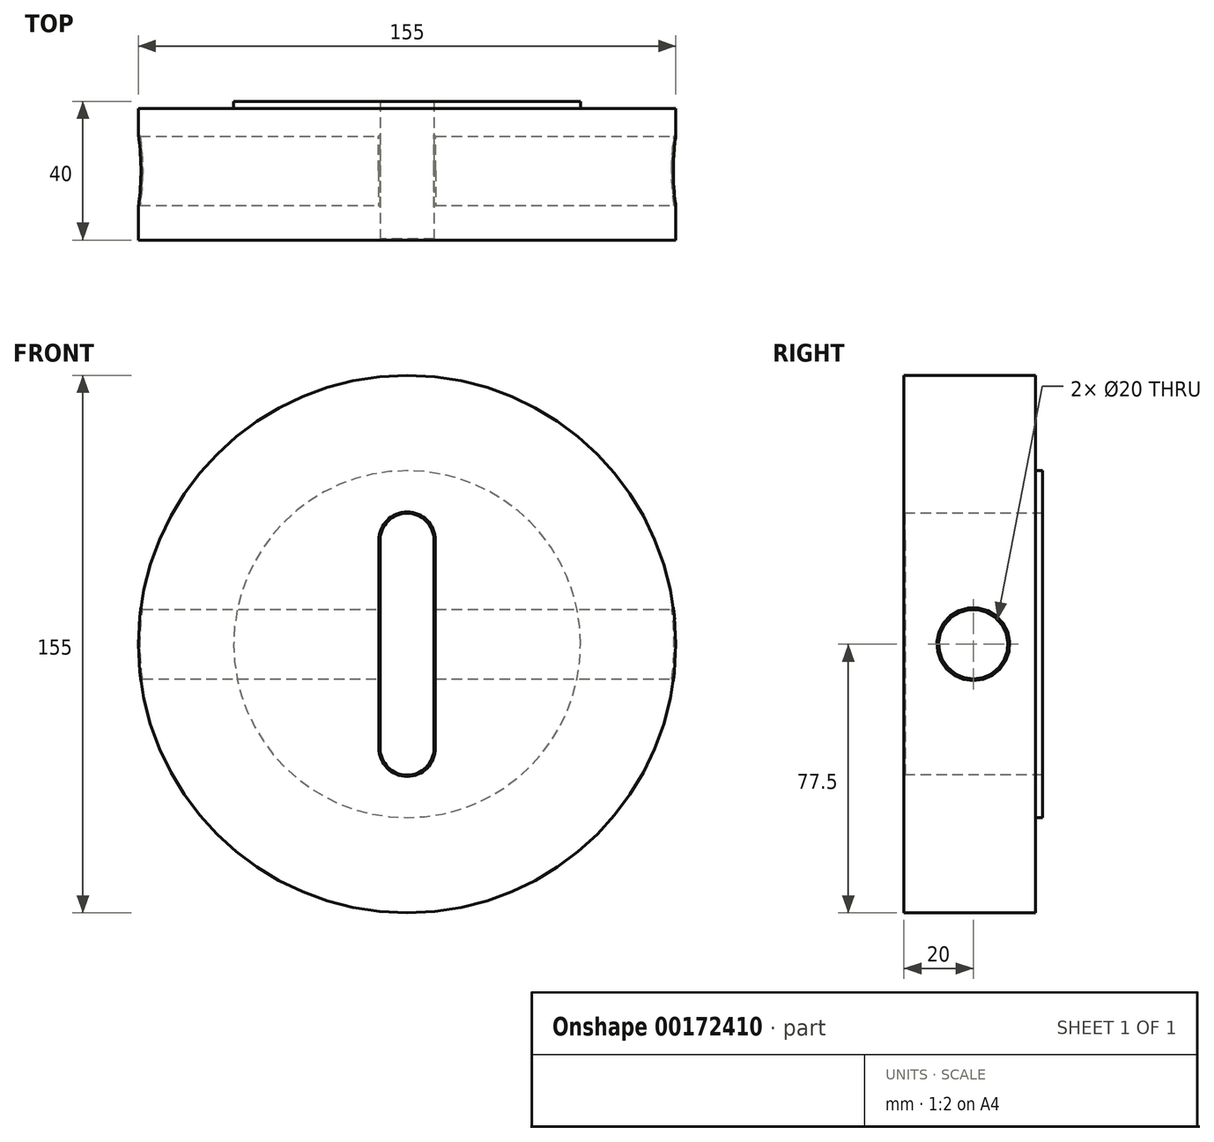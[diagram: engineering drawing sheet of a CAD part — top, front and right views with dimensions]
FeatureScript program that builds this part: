
annotation { "Feature Type Name" : "Feature", "Feature Type Description" : "" }
export const myFeature = defineFeature(function(context is Context, id is Id, definition is map)
    precondition{}
    {
        {
            var Q0;
            Q0=qCreatedBy(makeId("Front.planeOp"),FACE);
            var sketch = newSketch(context, id + "F0", { "sketchPlane" : qUnion([Q0])});
            skCircle(sketch, "E0", {"center": v(0, 0) * mm, "radius": 77.5 * mm});
            skCircle(sketch, "E1", {"center": v(0, 0) * mm, "radius": 50 * mm});
            skLineSegment(sketch, "E2", {"start": v(0, 0) * mm, "end": v(0, 30) * mm, "construction": true});
            skLineSegment(sketch, "E3", {"start": v(0, 0) * mm, "end": v(0, -30) * mm, "construction": true});
            skArc(sketch, "E4", {"start": v(7.75, 30) * mm, "mid": v(0, 37.75) * mm, "end": v(-7.75, 30) * mm});
            skArc(sketch, "E5", {"start": v(7.75, -30) * mm, "mid": v(0, -37.75) * mm, "end": v(-7.75, -30) * mm});
            skLineSegment(sketch, "E6", {"start": v(-7.75, 30) * mm, "end": v(-7.75, -30) * mm});
            skLineSegment(sketch, "E7", {"start": v(7.75, 30) * mm, "end": v(7.75, -30) * mm});
            skSolve(sketch);
        }
        {
            var Q0;
            Q0=makeQuery(id+"F0.imprint","IMPRINT",FACE,{"disambiguationData":[TD([[makeQuery(id+"F0.imprint","IMPRINT",EDGE,{"derivedFrom":sQuery(id+"F0.wireOp",EDGE,"E0")}),1.0]])]});
            extrude(context, id + "F1", {"entities" : qUnion([Q0]), "oppositeDirection" : true, "depth" : 38 * mm});
        }
        {
            var Q0;
            Q0=makeQuery(id+"F0.imprint","IMPRINT",FACE,{"disambiguationData":[TD([[makeQuery(id+"F0.imprint","IMPRINT",EDGE,{"derivedFrom":sQuery(id+"F0.wireOp",EDGE,"E1")}),1.0]])]});
            extrude(context, id + "F2", {"entities" : qUnion([Q0]), "operationType" : NewBodyOperationType.ADD, "oppositeDirection" : true, "depth" : 40 * mm});
        }
        {
            var Q0;
            Q0=qCreatedBy(makeId("Right.planeOp"),FACE);
            var sketch = newSketch(context, id + "F3", { "sketchPlane" : qUnion([Q0])});
            skCircle(sketch, "E8", {"center": v(20, 0) * mm, "radius": 10 * mm});
            skSolve(sketch);
        }
        {
            var Q0;
            Q0=makeQuery(id+"F3.imprint","IMPRINT",FACE,{"disambiguationData":[TD([[makeQuery(id+"F3.imprint","IMPRINT",EDGE,{"derivedFrom":sQuery(id+"F3.wireOp",EDGE,"E8")}),1.0]])]});
            extrude(context, id + "F4", {"entities" : qUnion([Q0]), "operationType" : NewBodyOperationType.REMOVE, "endBound" : BoundingType.THROUGH_ALL, "oppositeDirection" : true, "depth" : 25 * mm, "hasSecondDirection" : true, "secondDirectionBound" : SecondDirectionBoundingType.THROUGH_ALL, "secondDirectionOppositeDirection" : false, "secondDirectionDepth" : 25 * mm});
        }
        {
            var Q0;
            Q0=makeQuery(id+"F4.boolean.opBoolean","INTERSECT",EDGE,{"derivedFrom":[makeQuery(id+"F2.opExtrude","SWEPT_FACE",FACE,{"disambiguationData":[OSD([sQuery(id+"F0.wireOp",EDGE,"E7")])]}),makeQuery(id+"F4.opExtrude","SWEPT_FACE",FACE,{"disambiguationData":[OSD([sQuery(id+"F3.wireOp",EDGE,"E8")])]})]});
            var Q1;
            Q1=makeQuery(id+"F4.boolean.opBoolean","INTERSECT",EDGE,{"disambiguationData":[OD(1.0)],"derivedFrom":[makeQuery(id+"F1.opExtrude","SWEPT_FACE",FACE,{"disambiguationData":[OSD([sQuery(id+"F0.wireOp",EDGE,"E0")])]}),makeQuery(id+"F4.opExtrude","SWEPT_FACE",FACE,{"disambiguationData":[OSD([sQuery(id+"F3.wireOp",EDGE,"E8")])]})]});
            var Q2;
            Q2=makeQuery(id+"F4.boolean.opBoolean","INTERSECT",EDGE,{"derivedFrom":[makeQuery(id+"F2.opExtrude","SWEPT_FACE",FACE,{"disambiguationData":[OSD([sQuery(id+"F0.wireOp",EDGE,"E6")])]}),makeQuery(id+"F4.opExtrude","SWEPT_FACE",FACE,{"disambiguationData":[OSD([sQuery(id+"F3.wireOp",EDGE,"E8")])]})]});
            var Q3;
            Q3=makeQuery(id+"F4.boolean.opBoolean","INTERSECT",EDGE,{"disambiguationData":[OD(0.0)],"derivedFrom":[makeQuery(id+"F1.opExtrude","SWEPT_FACE",FACE,{"disambiguationData":[OSD([sQuery(id+"F0.wireOp",EDGE,"E0")])]}),makeQuery(id+"F4.opExtrude","SWEPT_FACE",FACE,{"disambiguationData":[OSD([sQuery(id+"F3.wireOp",EDGE,"E8")])]})]});
            chamfer(context, id + "F5", {"entities" : qUnion([Q0, Q1, Q2, Q3]), "width" : 0.5 * mm, "tangentPropagation" : true});
        }
        {
            var Q0;
            Q0=makeQuery(id+"F2.opExtrude","CAP_EDGE",EDGE,{"disambiguationData":[OSD([sQuery(id+"F0.wireOp",EDGE,"E6")])],"isStart":true});
            var Q1;
            Q1=makeQuery(id+"F2.opExtrude","CAP_EDGE",EDGE,{"disambiguationData":[OSD([sQuery(id+"F0.wireOp",EDGE,"E5")])],"isStart":true});
            var Q2;
            Q2=makeQuery(id+"F2.opExtrude","CAP_EDGE",EDGE,{"disambiguationData":[OSD([sQuery(id+"F0.wireOp",EDGE,"E7")])],"isStart":true});
            var Q3;
            Q3=makeQuery(id+"F2.opExtrude","CAP_EDGE",EDGE,{"disambiguationData":[OSD([sQuery(id+"F0.wireOp",EDGE,"E4")])],"isStart":true});
            chamfer(context, id + "F6", {"entities" : qUnion([Q0, Q1, Q2, Q3]), "width" : 0.4 * mm, "tangentPropagation" : true});
        }
    });
